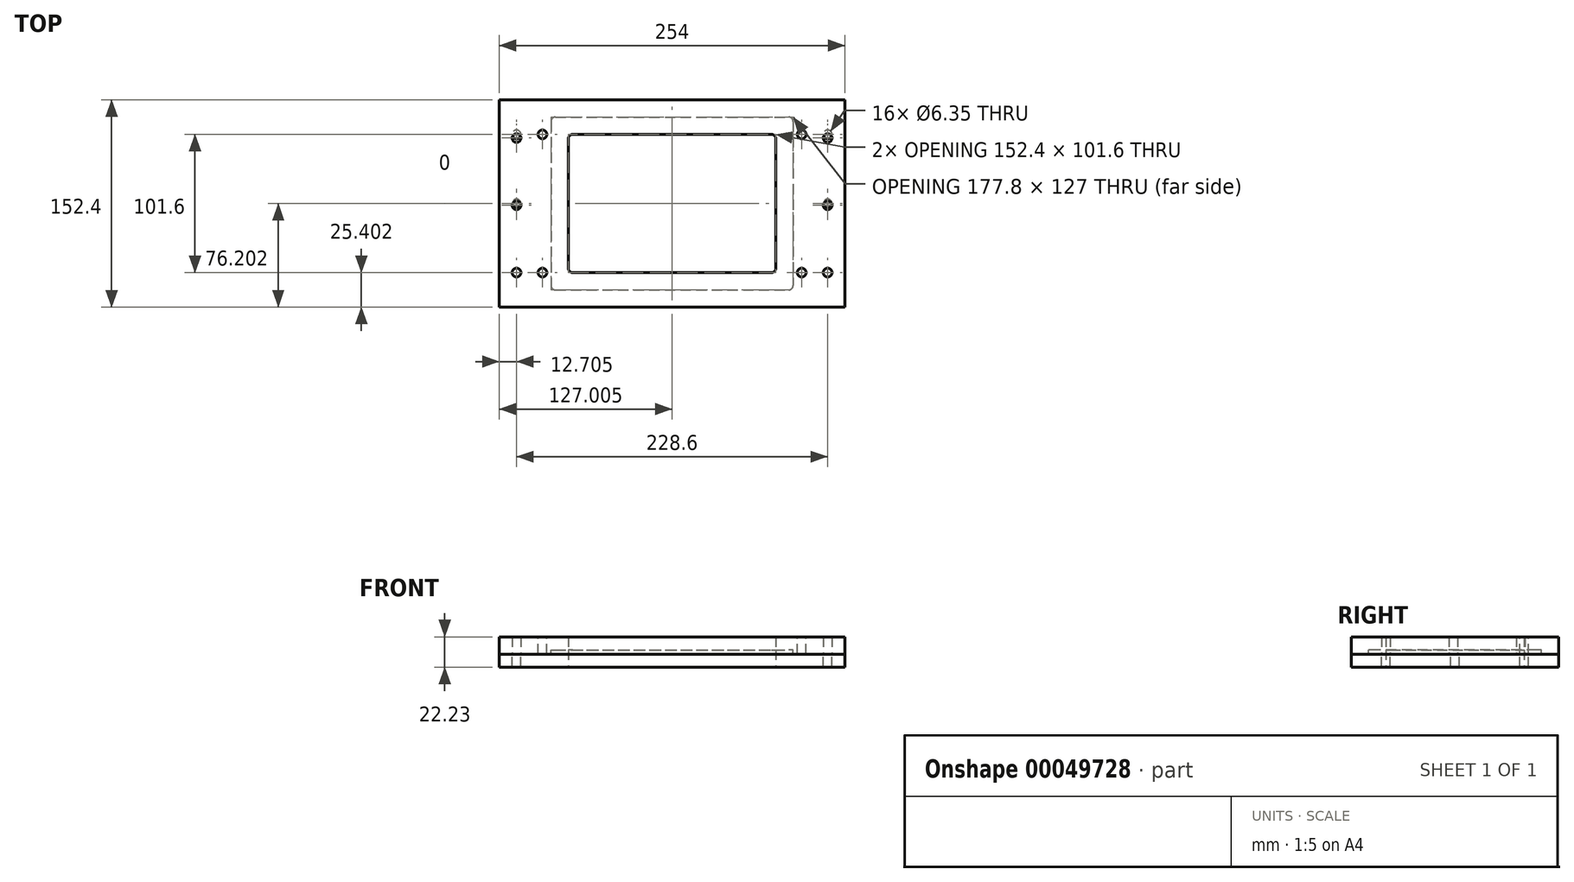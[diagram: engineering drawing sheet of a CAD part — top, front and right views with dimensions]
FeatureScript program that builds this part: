
annotation { "Feature Type Name" : "Feature", "Feature Type Description" : "" }
export const myFeature = defineFeature(function(context is Context, id is Id, definition is map)
    precondition{}
    {
        {
            var Q0;
            Q0=qCreatedBy(makeId("Top.planeOp"),FACE);
            var sketch = newSketch(context, id + "F0", { "sketchPlane" : qUnion([Q0])});
            skLineSegment(sketch, "E0.bottom", {"start": v(-55.24, 49.58) * mm, "end": v(97.16, 49.58) * mm});
            skLineSegment(sketch, "E0.top", {"start": v(-55.24, -52.02) * mm, "end": v(97.16, -52.02) * mm});
            skLineSegment(sketch, "E0.left", {"start": v(-55.24, 49.58) * mm, "end": v(-55.24, -52.02) * mm});
            skLineSegment(sketch, "E0.right", {"start": v(97.16, 49.58) * mm, "end": v(97.16, -52.02) * mm});
            skLineSegment(sketch, "E1.bottom", {"start": v(-106.04, 74.98) * mm, "end": v(147.96, 74.98) * mm});
            skLineSegment(sketch, "E1.top", {"start": v(-106.04, -77.42) * mm, "end": v(147.96, -77.42) * mm});
            skLineSegment(sketch, "E1.left", {"start": v(-106.04, 74.98) * mm, "end": v(-106.04, -77.42) * mm});
            skLineSegment(sketch, "E1.right", {"start": v(147.96, 74.98) * mm, "end": v(147.96, -77.42) * mm});
            skSolve(sketch);
        }
        {
            var Q0;
            Q0=makeQuery(id+"F0.imprint","IMPRINT",FACE,{"disambiguationData":[TD([[makeQuery(id+"F0.imprint","IMPRINT",EDGE,{"derivedFrom":sQuery(id+"F0.wireOp",EDGE,"E0.bottom")}),1.0]])]});
            extrude(context, id + "F1", {"entities" : qUnion([Q0]), "depth" : 12.7 * mm});
        }
        {
            var Q0;
            Q0=makeQuery(id+"F1.opExtrude","CAP_FACE",FACE,{"disambiguationData":[OSD([sQuery(id+"F0.wireOp",EDGE,"E0.bottom"),sQuery(id+"F0.wireOp",EDGE,"E0.top"),sQuery(id+"F0.wireOp",EDGE,"E0.left"),sQuery(id+"F0.wireOp",EDGE,"E0.right"),sQuery(id+"F0.wireOp",EDGE,"E1.bottom"),sQuery(id+"F0.wireOp",EDGE,"E1.top"),sQuery(id+"F0.wireOp",EDGE,"E1.left"),sQuery(id+"F0.wireOp",EDGE,"E1.right")])],"isStart":false});
            var sketch = newSketch(context, id + "F2", { "sketchPlane" : qUnion([Q0])});
            skLineSegment(sketch, "E2.bottom", {"start": v(-106.04, 74.98) * mm, "end": v(147.96, 74.98) * mm});
            skLineSegment(sketch, "E2.top", {"start": v(-106.04, -77.42) * mm, "end": v(147.96, -77.42) * mm});
            skLineSegment(sketch, "E2.left", {"start": v(-106.04, 74.98) * mm, "end": v(-106.04, -77.42) * mm});
            skLineSegment(sketch, "E2.right", {"start": v(147.96, 74.98) * mm, "end": v(147.96, -77.42) * mm});
            skLineSegment(sketch, "E3.bottom", {"start": v(-67.94, 62.28) * mm, "end": v(109.86, 62.28) * mm});
            skLineSegment(sketch, "E3.top", {"start": v(-67.94, -64.72) * mm, "end": v(109.86, -64.72) * mm});
            skLineSegment(sketch, "E3.left", {"start": v(-67.94, 62.28) * mm, "end": v(-67.94, -64.72) * mm});
            skLineSegment(sketch, "E3.right", {"start": v(109.86, 62.28) * mm, "end": v(109.86, -64.72) * mm});
            skSolve(sketch);
        }
        {
            var Q0;
            Q0=makeQuery(id+"F2.imprint","IMPRINT",FACE,{"disambiguationData":[TD([[makeQuery(id+"F2.imprint","IMPRINT",EDGE,{"derivedFrom":sQuery(id+"F2.wireOp",EDGE,"E2.bottom")}),-1.0]])]});
            extrude(context, id + "F3", {"entities" : qUnion([Q0]), "operationType" : NewBodyOperationType.REMOVE, "oppositeDirection" : true, "depth" : 3.17 * mm});
        }
        {
            var Q0;
            Q0=makeQuery(id+"F1.opExtrude","SWEPT_EDGE",EDGE,{"disambiguationData":[OSD([sQuery(id+"F0.wireOp",EDGE,"E0.bottom"),sQuery(id+"F0.wireOp",EDGE,"E0.left")])]});
            var Q1;
            Q1=makeQuery(id+"F1.opExtrude","SWEPT_EDGE",EDGE,{"disambiguationData":[OSD([sQuery(id+"F0.wireOp",EDGE,"E0.top"),sQuery(id+"F0.wireOp",EDGE,"E0.left")])]});
            var Q2;
            Q2=makeQuery(id+"F1.opExtrude","SWEPT_EDGE",EDGE,{"disambiguationData":[OSD([sQuery(id+"F0.wireOp",EDGE,"E0.top"),sQuery(id+"F0.wireOp",EDGE,"E0.right")])]});
            var Q3;
            Q3=makeQuery(id+"F1.opExtrude","SWEPT_EDGE",EDGE,{"disambiguationData":[OSD([sQuery(id+"F0.wireOp",EDGE,"E0.bottom"),sQuery(id+"F0.wireOp",EDGE,"E0.right")])]});
            fillet(context, id + "F4", {"entities" : qUnion([Q0, Q1, Q2, Q3]), "radius" : 3.17 * mm, "tangentPropagation" : true, "allowEdgeOverflow" : false});
        }
        {
            var Q0;
            Q0=makeQuery(id+"F3.boolean.opBoolean","COPY",FACE,{"derivedFrom":makeQuery(id+"F3.opExtrude","CAP_FACE",FACE,{"disambiguationData":[OSD([sQuery(id+"F2.wireOp",EDGE,"E2.bottom"),sQuery(id+"F2.wireOp",EDGE,"E2.top"),sQuery(id+"F2.wireOp",EDGE,"E2.left"),sQuery(id+"F2.wireOp",EDGE,"E2.right"),sQuery(id+"F2.wireOp",EDGE,"E3.bottom"),sQuery(id+"F2.wireOp",EDGE,"E3.top"),sQuery(id+"F2.wireOp",EDGE,"E3.left"),sQuery(id+"F2.wireOp",EDGE,"E3.right")])],"isStart":false})});
            var sketch = newSketch(context, id + "F5", { "sketchPlane" : qUnion([Q0])});
            skPoint(sketch, "E4", {"position": v(135.26, -52.02) * mm});
            skPoint(sketch, "E5", {"position": v(-93.34, -52.02) * mm});
            skPoint(sketch, "E6", {"position": v(-93.34, 49.58) * mm});
            skPoint(sketch, "E7", {"position": v(135.26, 49.58) * mm});
            skPoint(sketch, "E8", {"position": v(-93.34, -1.22) * mm});
            skPoint(sketch, "E9", {"position": v(135.26, -1.22) * mm});
            skSolve(sketch);
        }
        {
            var Q0;
            Q0=sQuery(id+"F5.wireOp",VERTEX,"E7");
            var Q1;
            Q1=sQuery(id+"F5.wireOp",VERTEX,"E9");
            var Q2;
            Q2=sQuery(id+"F5.wireOp",VERTEX,"E4");
            var Q3;
            Q3=sQuery(id+"F5.wireOp",VERTEX,"E8");
            var Q4;
            Q4=sQuery(id+"F5.wireOp",VERTEX,"E5");
            var Q5;
            Q5=sQuery(id+"F5.wireOp",VERTEX,"E6");
            var Q6;
            Q6=makeQuery(id+"F1.opExtrude","SWEPT_BODY",BODY,{"disambiguationData":[OSD([sQuery(id+"F0.wireOp",EDGE,"E0.bottom"),sQuery(id+"F0.wireOp",EDGE,"E0.top"),sQuery(id+"F0.wireOp",EDGE,"E0.left"),sQuery(id+"F0.wireOp",EDGE,"E0.right"),sQuery(id+"F0.wireOp",EDGE,"E1.bottom"),sQuery(id+"F0.wireOp",EDGE,"E1.top"),sQuery(id+"F0.wireOp",EDGE,"E1.left"),sQuery(id+"F0.wireOp",EDGE,"E1.right")])]});
            hole(context, id + "F6", {"style" : HoleStyle.SIMPLE, "holeDiameter" : 6.35 * mm, "endStyle" : HoleEndStyle.THROUGH, "locations" : qUnion([Q0, Q1, Q2, Q3, Q4, Q5]), "scope" : qUnion([Q6])});
        }
        {
            var Q0;
            Q0=makeQuery(id+"F3.boolean.opBoolean","COPY",EDGE,{"derivedFrom":makeQuery(id+"F3.opExtrude","SWEPT_EDGE",EDGE,{"disambiguationData":[OSD([sQuery(id+"F2.wireOp",EDGE,"E3.bottom"),sQuery(id+"F2.wireOp",EDGE,"E3.right")])]})});
            var Q1;
            Q1=makeQuery(id+"F3.boolean.opBoolean","COPY",EDGE,{"derivedFrom":makeQuery(id+"F3.opExtrude","SWEPT_EDGE",EDGE,{"disambiguationData":[OSD([sQuery(id+"F2.wireOp",EDGE,"E3.bottom"),sQuery(id+"F2.wireOp",EDGE,"E3.left")])]})});
            var Q2;
            Q2=makeQuery(id+"F3.boolean.opBoolean","COPY",EDGE,{"derivedFrom":makeQuery(id+"F3.opExtrude","SWEPT_EDGE",EDGE,{"disambiguationData":[OSD([sQuery(id+"F2.wireOp",EDGE,"E3.top"),sQuery(id+"F2.wireOp",EDGE,"E3.left")])]})});
            var Q3;
            Q3=makeQuery(id+"F3.boolean.opBoolean","COPY",EDGE,{"derivedFrom":makeQuery(id+"F3.opExtrude","SWEPT_EDGE",EDGE,{"disambiguationData":[OSD([sQuery(id+"F2.wireOp",EDGE,"E3.top"),sQuery(id+"F2.wireOp",EDGE,"E3.right")])]})});
            fillet(context, id + "F7", {"entities" : qUnion([Q0, Q1, Q2, Q3]), "radius" : 3.17 * mm, "tangentPropagation" : true, "allowEdgeOverflow" : false});
        }
        {
            var Q0;
            Q0=makeQuery(id+"F3.boolean.opBoolean","COPY",FACE,{"derivedFrom":makeQuery(id+"F3.opExtrude","CAP_FACE",FACE,{"disambiguationData":[OSD([sQuery(id+"F2.wireOp",EDGE,"E2.bottom"),sQuery(id+"F2.wireOp",EDGE,"E2.top"),sQuery(id+"F2.wireOp",EDGE,"E2.left"),sQuery(id+"F2.wireOp",EDGE,"E2.right"),sQuery(id+"F2.wireOp",EDGE,"E3.bottom"),sQuery(id+"F2.wireOp",EDGE,"E3.top"),sQuery(id+"F2.wireOp",EDGE,"E3.left"),sQuery(id+"F2.wireOp",EDGE,"E3.right")])],"isStart":false})});
            var sketch = newSketch(context, id + "F8", { "sketchPlane" : qUnion([Q0])});
            skLineSegment(sketch, "E10.bottom", {"start": v(147.96, -77.42) * mm, "end": v(-106.04, -77.42) * mm});
            skLineSegment(sketch, "E10.top", {"start": v(147.96, 74.98) * mm, "end": v(-106.04, 74.98) * mm});
            skLineSegment(sketch, "E10.left", {"start": v(147.96, -77.42) * mm, "end": v(147.96, 74.98) * mm});
            skLineSegment(sketch, "E10.right", {"start": v(-106.04, -77.42) * mm, "end": v(-106.04, 74.98) * mm});
            skLineSegment(sketch, "E11.bottom", {"start": v(97.16, -52.02) * mm, "end": v(-55.24, -52.02) * mm});
            skLineSegment(sketch, "E11.top", {"start": v(97.16, 49.58) * mm, "end": v(-55.24, 49.58) * mm});
            skLineSegment(sketch, "E11.left", {"start": v(97.16, -52.02) * mm, "end": v(97.16, 49.58) * mm});
            skLineSegment(sketch, "E11.right", {"start": v(-55.24, -52.02) * mm, "end": v(-55.24, 49.58) * mm});
            skSolve(sketch);
        }
        {
            var Q0;
            Q0 = qSketchRegion(id + "F8", true);
            extrude(context, id + "F9", {"entities" : qUnion([Q0]), "depth" : 12.7 * mm});
        }
        {
            var Q0;
            Q0=makeQuery(id+"F1.opExtrude","SWEPT_BODY",BODY,{"disambiguationData":[OSD([sQuery(id+"F0.wireOp",EDGE,"E0.bottom"),sQuery(id+"F0.wireOp",EDGE,"E0.top"),sQuery(id+"F0.wireOp",EDGE,"E0.left"),sQuery(id+"F0.wireOp",EDGE,"E0.right"),sQuery(id+"F0.wireOp",EDGE,"E1.bottom"),sQuery(id+"F0.wireOp",EDGE,"E1.top"),sQuery(id+"F0.wireOp",EDGE,"E1.left"),sQuery(id+"F0.wireOp",EDGE,"E1.right")])]});
            var Q1;
            Q1=makeQuery(id+"F9.opExtrude","SWEPT_BODY",BODY,{"disambiguationData":[OSD([sQuery(id+"F8.wireOp",EDGE,"E10.bottom"),sQuery(id+"F8.wireOp",EDGE,"E10.top"),sQuery(id+"F8.wireOp",EDGE,"E10.left"),sQuery(id+"F8.wireOp",EDGE,"E10.right"),sQuery(id+"F8.wireOp",EDGE,"E11.bottom"),sQuery(id+"F8.wireOp",EDGE,"E11.top"),sQuery(id+"F8.wireOp",EDGE,"E11.left"),sQuery(id+"F8.wireOp",EDGE,"E11.right")])]});
            booleanBodies(context, id + "F10", {"operationType" : BooleanOperationType.SUBTRACTION, "tools" : qUnion([Q0]), "targets" : qUnion([Q1]), "keepTools" : true});
        }
        {
            var Q0;
            Q0=makeQuery(id+"F9.opExtrude","SWEPT_EDGE",EDGE,{"disambiguationData":[OSD([sQuery(id+"F8.wireOp",EDGE,"E11.bottom"),sQuery(id+"F8.wireOp",EDGE,"E11.left")])]});
            var Q1;
            Q1=makeQuery(id+"F9.opExtrude","SWEPT_EDGE",EDGE,{"disambiguationData":[OSD([sQuery(id+"F8.wireOp",EDGE,"E11.top"),sQuery(id+"F8.wireOp",EDGE,"E11.left")])]});
            var Q2;
            Q2=makeQuery(id+"F9.opExtrude","SWEPT_EDGE",EDGE,{"disambiguationData":[OSD([sQuery(id+"F8.wireOp",EDGE,"E11.top"),sQuery(id+"F8.wireOp",EDGE,"E11.right")])]});
            var Q3;
            Q3=makeQuery(id+"F9.opExtrude","SWEPT_EDGE",EDGE,{"disambiguationData":[OSD([sQuery(id+"F8.wireOp",EDGE,"E11.bottom"),sQuery(id+"F8.wireOp",EDGE,"E11.right")])]});
            fillet(context, id + "F11", {"entities" : qUnion([Q0, Q1, Q2, Q3]), "radius" : 3.17 * mm, "tangentPropagation" : true, "allowEdgeOverflow" : false});
        }
        {
            var Q0;
            Q0=makeQuery(id+"F9.opExtrude","CAP_FACE",FACE,{"disambiguationData":[OSD([sQuery(id+"F8.wireOp",EDGE,"E10.bottom"),sQuery(id+"F8.wireOp",EDGE,"E10.top"),sQuery(id+"F8.wireOp",EDGE,"E10.left"),sQuery(id+"F8.wireOp",EDGE,"E10.right"),sQuery(id+"F8.wireOp",EDGE,"E11.bottom"),sQuery(id+"F8.wireOp",EDGE,"E11.top"),sQuery(id+"F8.wireOp",EDGE,"E11.left"),sQuery(id+"F8.wireOp",EDGE,"E11.right")])],"isStart":true});
            var sketch = newSketch(context, id + "F12", { "sketchPlane" : qUnion([Q0])});
            skPoint(sketch, "E12", {"position": v(135.26, -46.9) * mm});
            skPoint(sketch, "E13", {"position": v(-93.34, -46.9) * mm});
            skPoint(sketch, "E14", {"position": v(-93.34, 52.02) * mm});
            skPoint(sketch, "E15", {"position": v(135.26, 52.02) * mm});
            skPoint(sketch, "E16", {"position": v(-93.34, 2.56) * mm});
            skPoint(sketch, "E17", {"position": v(135.26, 2.56) * mm});
            skSolve(sketch);
        }
        {
            var Q0;
            Q0=sQuery(id+"F12.wireOp",VERTEX,"E14");
            var Q1;
            Q1=sQuery(id+"F12.wireOp",VERTEX,"E16");
            var Q2;
            Q2=sQuery(id+"F12.wireOp",VERTEX,"E13");
            var Q3;
            Q3=sQuery(id+"F12.wireOp",VERTEX,"E15");
            var Q4;
            Q4=sQuery(id+"F12.wireOp",VERTEX,"E17");
            var Q5;
            Q5=sQuery(id+"F12.wireOp",VERTEX,"E12");
            var Q6;
            Q6=makeQuery(id+"F9.opExtrude","SWEPT_BODY",BODY,{"disambiguationData":[OSD([sQuery(id+"F8.wireOp",EDGE,"E10.bottom"),sQuery(id+"F8.wireOp",EDGE,"E10.top"),sQuery(id+"F8.wireOp",EDGE,"E10.left"),sQuery(id+"F8.wireOp",EDGE,"E10.right"),sQuery(id+"F8.wireOp",EDGE,"E11.bottom"),sQuery(id+"F8.wireOp",EDGE,"E11.top"),sQuery(id+"F8.wireOp",EDGE,"E11.left"),sQuery(id+"F8.wireOp",EDGE,"E11.right")])]});
            hole(context, id + "F13", {"style" : HoleStyle.SIMPLE, "holeDiameter" : 6.35 * mm, "endStyle" : HoleEndStyle.THROUGH, "locations" : qUnion([Q0, Q1, Q2, Q3, Q4, Q5]), "scope" : qUnion([Q6])});
        }
        {
            var Q0;
            Q0=makeQuery(id+"F9.opExtrude","CAP_FACE",FACE,{"disambiguationData":[OSD([sQuery(id+"F8.wireOp",EDGE,"E10.bottom"),sQuery(id+"F8.wireOp",EDGE,"E10.top"),sQuery(id+"F8.wireOp",EDGE,"E10.left"),sQuery(id+"F8.wireOp",EDGE,"E10.right"),sQuery(id+"F8.wireOp",EDGE,"E11.bottom"),sQuery(id+"F8.wireOp",EDGE,"E11.top"),sQuery(id+"F8.wireOp",EDGE,"E11.left"),sQuery(id+"F8.wireOp",EDGE,"E11.right")])],"isStart":false});
            var sketch = newSketch(context, id + "F14", { "sketchPlane" : qUnion([Q0])});
            skPoint(sketch, "E18", {"position": v(-74.29, 49.58) * mm});
            skPoint(sketch, "E19", {"position": v(-74.29, -52.02) * mm});
            skPoint(sketch, "E20", {"position": v(116.21, -52.02) * mm});
            skPoint(sketch, "E21", {"position": v(116.21, 49.58) * mm});
            skSolve(sketch);
        }
        {
            var Q0;
            Q0=sQuery(id+"F14.wireOp",VERTEX,"E18");
            var Q1;
            Q1=sQuery(id+"F14.wireOp",VERTEX,"E19");
            var Q2;
            Q2=sQuery(id+"F14.wireOp",VERTEX,"E20");
            var Q3;
            Q3=sQuery(id+"F14.wireOp",VERTEX,"E21");
            var Q4;
            Q4=makeQuery(id+"F9.opExtrude","SWEPT_BODY",BODY,{"disambiguationData":[OSD([sQuery(id+"F8.wireOp",EDGE,"E10.bottom"),sQuery(id+"F8.wireOp",EDGE,"E10.top"),sQuery(id+"F8.wireOp",EDGE,"E10.left"),sQuery(id+"F8.wireOp",EDGE,"E10.right"),sQuery(id+"F8.wireOp",EDGE,"E11.bottom"),sQuery(id+"F8.wireOp",EDGE,"E11.top"),sQuery(id+"F8.wireOp",EDGE,"E11.left"),sQuery(id+"F8.wireOp",EDGE,"E11.right")])]});
            hole(context, id + "F15", {"style" : HoleStyle.SIMPLE, "holeDiameter" : 6.35 * mm, "endStyle" : HoleEndStyle.THROUGH, "locations" : qUnion([Q0, Q1, Q2, Q3]), "scope" : qUnion([Q4])});
        }
    });
